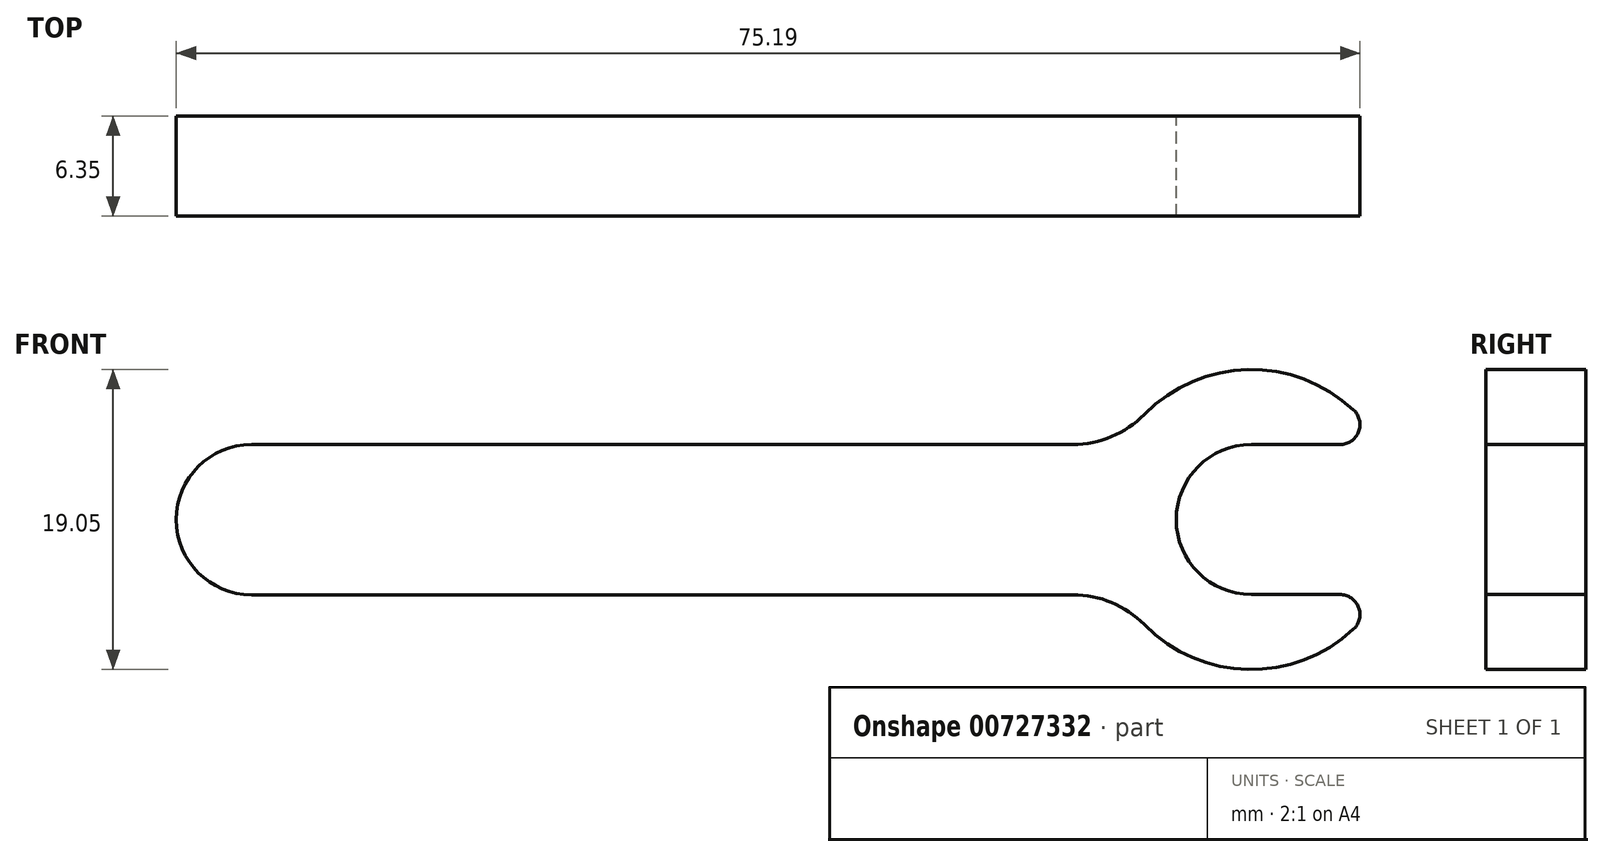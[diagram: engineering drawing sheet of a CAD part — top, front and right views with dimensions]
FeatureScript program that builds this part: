
annotation { "Feature Type Name" : "Feature", "Feature Type Description" : "" }
export const myFeature = defineFeature(function(context is Context, id is Id, definition is map)
    precondition{}
    {
        {
            var Q0;
            Q0=qCreatedBy(makeId("Front.planeOp"),FACE);
            var sketch = newSketch(context, id + "F0", { "sketchPlane" : qUnion([Q0])});
            skLineSegment(sketch, "E0", {"start": v(0, 4.78) * mm, "end": v(52.18, 4.78) * mm});
            skLineSegment(sketch, "E1", {"start": v(52.18, -4.78) * mm, "end": v(0, -4.78) * mm});
            skArc(sketch, "E2", {"start": v(0, 4.78) * mm, "mid": v(-4.78, 0) * mm, "end": v(0, -4.78) * mm});
            skArc(sketch, "E3", {"start": v(70, 6.96) * mm, "mid": v(63.3, 9.52) * mm, "end": v(56.7, 6.68) * mm});
            skArc(sketch, "E4", {"start": v(56.7, -6.68) * mm, "mid": v(63.3, -9.52) * mm, "end": v(70, -6.96) * mm});
            skArc(sketch, "E5", {"start": v(69.14, 4.76) * mm, "mid": v(70.32, 5.57) * mm, "end": v(70, 6.96) * mm});
            skLineSegment(sketch, "E6", {"start": v(69.14, -4.76) * mm, "end": v(63.5, -4.76) * mm});
            skLineSegment(sketch, "E7", {"start": v(69.14, 4.76) * mm, "end": v(63.5, 4.76) * mm});
            skArc(sketch, "E8", {"start": v(70, -6.96) * mm, "mid": v(70.32, -5.57) * mm, "end": v(69.14, -4.76) * mm});
            skArc(sketch, "E9", {"start": v(63.5, 4.76) * mm, "mid": v(58.74, 0) * mm, "end": v(63.5, -4.76) * mm});
            skLineSegment(sketch, "E10", {"start": v(-4.78, 0) * mm, "end": v(63.5, 0) * mm, "construction": true});
            skArc(sketch, "E11", {"start": v(52.18, 4.78) * mm, "mid": v(54.63, 5.27) * mm, "end": v(56.7, 6.68) * mm});
            skArc(sketch, "E12", {"start": v(56.7, -6.68) * mm, "mid": v(54.63, -5.27) * mm, "end": v(52.18, -4.78) * mm});
            skLineSegment(sketch, "E13", {"start": v(63.5, -9.53) * mm, "end": v(63.5, 9.53) * mm, "construction": true});
            skSolve(sketch);
        }
        {
            var Q0;
            Q0 = qSketchRegion(id + "F0", true);
            extrude(context, id + "F1", {"entities" : qUnion([Q0]), "depth" : 6.35 * mm, "offsetDistance" : 25.4 * mm});
        }
    });
